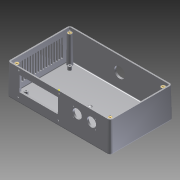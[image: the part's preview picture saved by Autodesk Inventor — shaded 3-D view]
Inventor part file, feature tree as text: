
AUTODESK INVENTOR PART (.ipt)
format: ipt  version: 2015 (Build 190159000, 159)  size: 571,392 bytes
history: native  units: in
note: dims shown in document units (in); Inventor stores cm internally (conversion verified against a paired STEP export)
features: sketch x6, imported_body x5, extrude x4, mirror x3, other x2, rib x1
ambient origin geometry x8: Origin, YZ Plane, XZ Plane, XY Plane, X Axis, Y Axis, Z Axis, Center Point
bodies: Body1 (feature_tree), Body2 (feature_tree), Body3 (feature_tree), Body4 (feature_tree), Body5 (feature_tree)
feature tree (21):
  rib  "Rib2"
  other  "DC-47B_DC-47BPMBY.ipt1"
  sketch  "Sketch1"  dims[d0=0.669in d1=0.669in]
  sketch  "Sketch2"  dims[d2=1.063in d3=0.7874in]
  extrude  "Extrusion2"  Depth=0.669in
  extrude  "Extrusion3"  Depth=0.7874in
  extrude  "Extrusion5"  Depth=0.7874in
  extrude  "Extrusion6"  Depth=0.787in
  other  "_INSERT_-_#4-40 Tapped Hole2_"
  mirror  "Mirror5"
  mirror  "Mirror6[1]"
  mirror  "Mirror6[2]"
  imported_body  "Base1"
  imported_body  "Base2"
  imported_body  "Base3"
  imported_body  "Base4"
  imported_body  "Base5"
  sketch  "Sketch3"  dims[d4=1.1811in d5=0.7874in]
  sketch  "Sketch4"  dims[d27=1.772in d28=0.787in]
  sketch  "Sketch7"  dims[d29=0.354in]
  sketch  "Sketch8"  dims[d30=0.394in d31=0.079in d32=0.0585in d33=0.059in d34=0.059in d35=0.059in d36=0.079in d37=0.0585in d38=0.059in d39=0.079in d40=0.079in d41=0.059in d42=0.059in d43=1.0in d44=0.0in d46=1.0827in d47=2.8543in d48=3.3125in d49=0.0in d59=0.1083in d60=0.0689in d61=0.3839in d62=0.3839in d63=1.7125in d64=1.7125in d65=2.9921in d66=2.815in d67=1.0433in d68=0.0197in d69=0.0197in d104=0.7874in d105=1.0678in d106=3.6245in d107=1.0in d108=0.0in d109=0.3937in d110=0.3937in d111=6.6929in d113=0.1969in d114=0.3937in d116=1.0in d118=0.4409in d119=0.1091in d120=0.1969in d121=0.0in]
